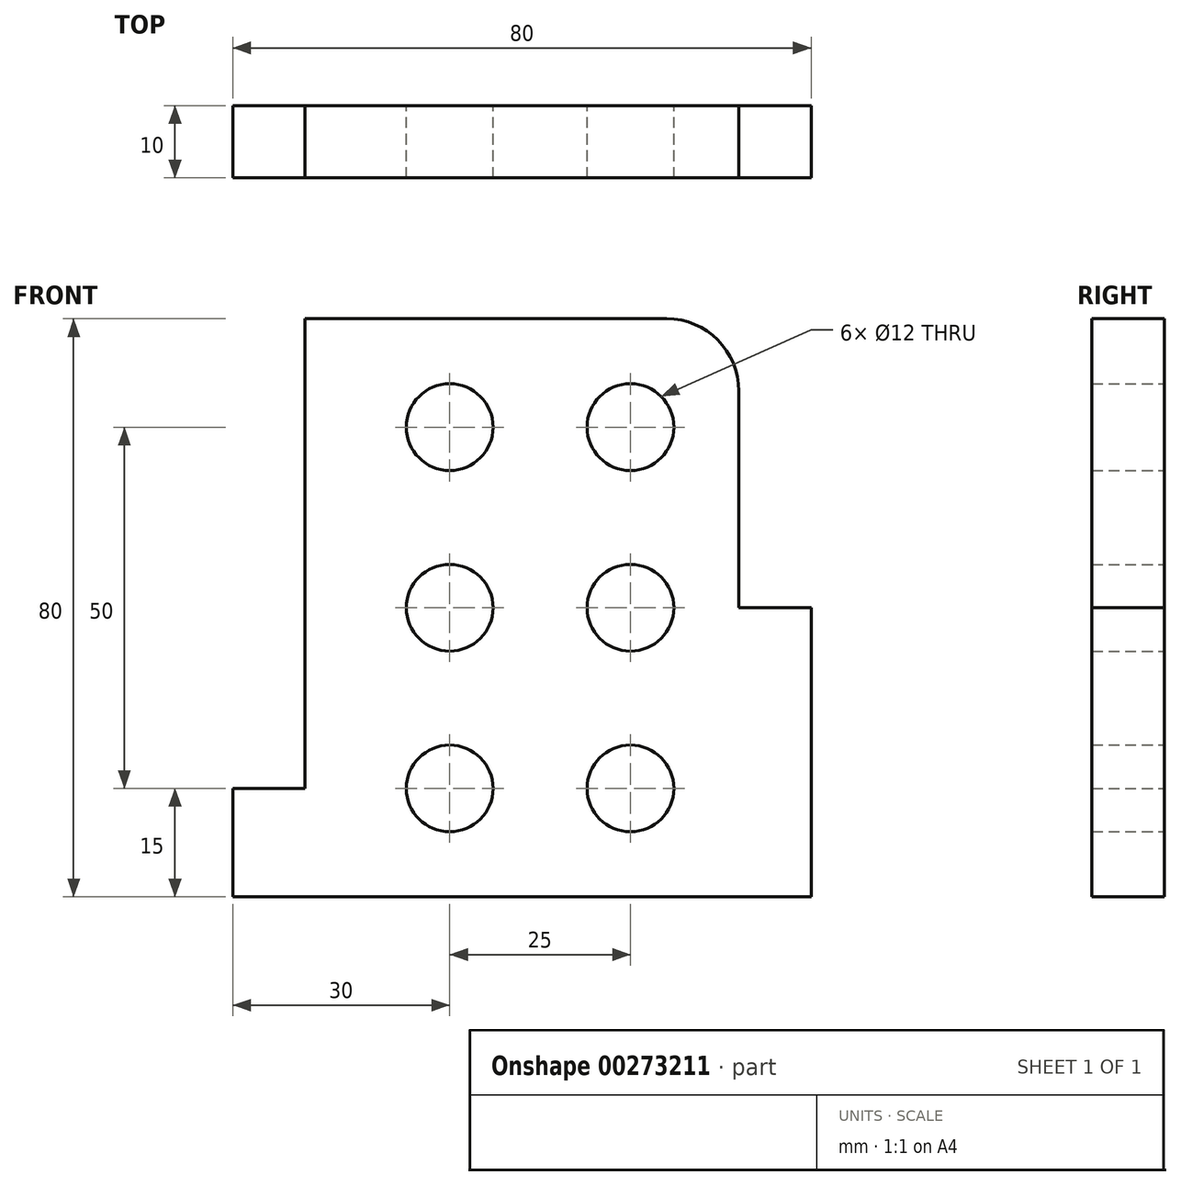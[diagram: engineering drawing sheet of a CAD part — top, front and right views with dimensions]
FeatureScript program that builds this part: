
annotation { "Feature Type Name" : "Feature", "Feature Type Description" : "" }
export const myFeature = defineFeature(function(context is Context, id is Id, definition is map)
    precondition{}
    {
        {
            var Q0;
            Q0=qCreatedBy(makeId("Front.planeOp"),FACE);
            var sketch = newSketch(context, id + "F0", { "sketchPlane" : qUnion([Q0])});
            skLineSegment(sketch, "E0", {"start": v(0, 0) * mm, "end": v(80, 0) * mm});
            skLineSegment(sketch, "E1", {"start": v(80, 0) * mm, "end": v(80, 40) * mm});
            skLineSegment(sketch, "E2", {"start": v(80, 40) * mm, "end": v(70, 40) * mm});
            skLineSegment(sketch, "E3", {"start": v(70, 40) * mm, "end": v(70, 70) * mm});
            skLineSegment(sketch, "E4", {"start": v(0, 0) * mm, "end": v(0, 15) * mm});
            skLineSegment(sketch, "E5", {"start": v(0, 15) * mm, "end": v(10, 15) * mm});
            skLineSegment(sketch, "E6", {"start": v(10, 15) * mm, "end": v(10, 80) * mm});
            skLineSegment(sketch, "E7", {"start": v(10, 80) * mm, "end": v(60, 80) * mm});
            skArc(sketch, "E8", {"start": v(70, 70) * mm, "mid": v(67.07, 77.07) * mm, "end": v(60, 80) * mm});
            skCircle(sketch, "E9", {"center": v(30, 15) * mm, "radius": 6 * mm});
            skCircle(sketch, "E10", {"center": v(55, 15) * mm, "radius": 6 * mm});
            skCircle(sketch, "E11", {"center": v(30, 40) * mm, "radius": 6 * mm});
            skCircle(sketch, "E12", {"center": v(55, 40) * mm, "radius": 6 * mm});
            skCircle(sketch, "E13", {"center": v(55, 65) * mm, "radius": 6 * mm});
            skCircle(sketch, "E14", {"center": v(30, 65) * mm, "radius": 6 * mm});
            skSolve(sketch);
        }
        {
            var Q0;
            Q0 = qSketchRegion(id + "F0", true);
            extrude(context, id + "F1", {"entities" : qUnion([Q0]), "depth" : 10 * mm});
        }
    });
